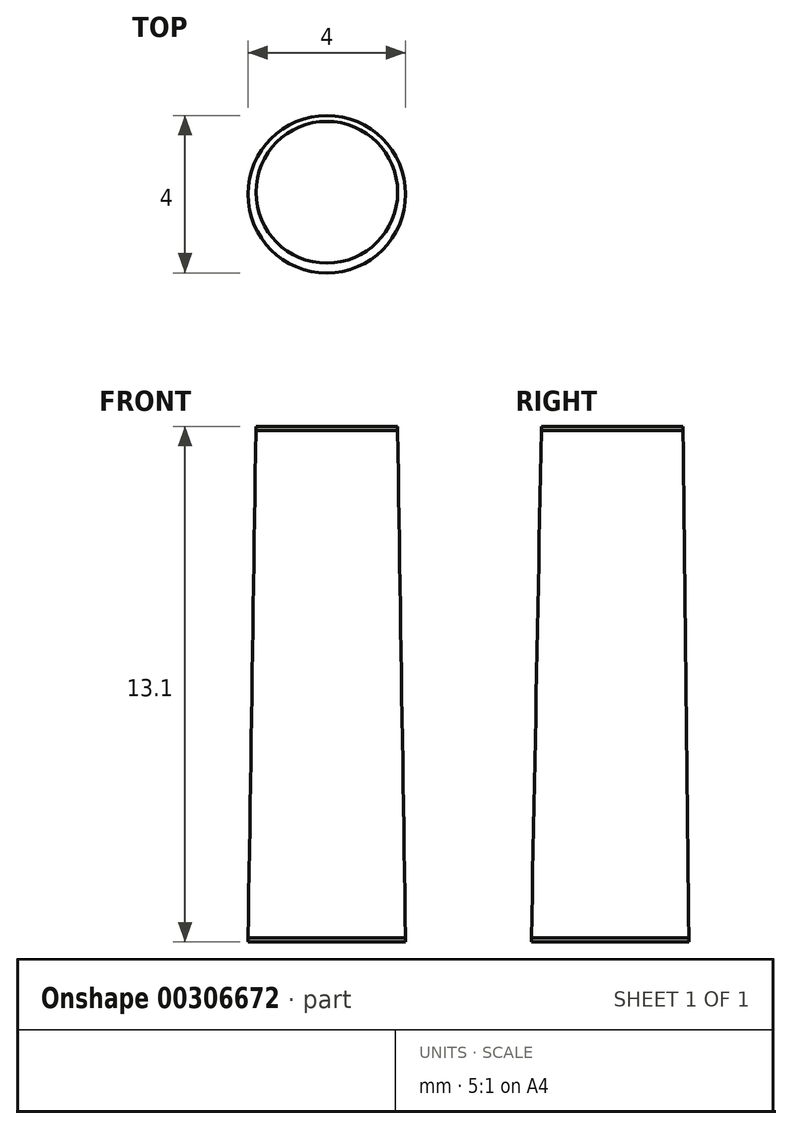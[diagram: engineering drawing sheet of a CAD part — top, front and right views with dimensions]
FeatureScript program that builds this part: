
annotation { "Feature Type Name" : "Feature", "Feature Type Description" : "" }
export const myFeature = defineFeature(function(context is Context, id is Id, definition is map)
    precondition{}
    {
        {
            var Q0;
            Q0=qCreatedBy(makeId("Top.planeOp"),FACE);
            var sketch = newSketch(context, id + "F0", { "sketchPlane" : qUnion([Q0])});
            skCircle(sketch, "E0", {"center": v(0, -0.05) * mm, "radius": 2 * mm});
            skSolve(sketch);
        }
        {
            var Q0;
            Q0=qCreatedBy(makeId("Top.planeOp"),FACE);
            var sketch = newSketch(context, id + "F1", { "sketchPlane" : qUnion([Q0])});
            skCircle(sketch, "E1", {"center": v(0, 0) * mm, "radius": 1.8 * mm});
            skSolve(sketch);
        }
        {
            var Q0;
            Q0=makeQuery(id+"F1.imprint","IMPRINT",FACE,{"disambiguationData":[TD([[makeQuery(id+"F1.imprint","IMPRINT",EDGE,{"derivedFrom":sQuery(id+"F1.wireOp",EDGE,"E1")}),1.0]])]});
            extrude(context, id + "F2", {"entities" : qUnion([Q0]), "depth" : 0.1 * mm});
        }
        {
            var Q0;
            Q0=makeQuery(id+"F2.opExtrude","SWEPT_BODY",BODY,{"disambiguationData":[OSD([sQuery(id+"F1.wireOp",EDGE,"E1")])]});
            transform(context, id + "F3", {"entities" : qUnion([Q0]), "transformType" : TransformType.TRANSLATION_3D, "dx" : 0 * mm, "dy" : 0 * mm, "dz" : 13 * mm, "makeCopy" : false});
        }
        {
            var Q0;
            Q0=makeQuery(id+"F0.imprint","IMPRINT",FACE,{"disambiguationData":[TD([[makeQuery(id+"F0.imprint","IMPRINT",EDGE,{"derivedFrom":sQuery(id+"F0.wireOp",EDGE,"E0")}),1.0]])]});
            var Q1;
            Q1 = qSketchRegion(id + "F0", true);
            extrude(context, id + "F4", {"entities" : qUnion([Q0, Q1]), "depth" : 0.1 * mm});
        }
        {
            var Q0;
            Q0=makeQuery(id+"F4.opExtrude","CAP_FACE",FACE,{"disambiguationData":[OSD([sQuery(id+"F0.wireOp",EDGE,"E0")])],"isStart":false});
            var Q1;
            Q1=makeQuery(id+"F2.opExtrude","CAP_FACE",FACE,{"disambiguationData":[OSD([sQuery(id+"F1.wireOp",EDGE,"E1")])],"isStart":true});
            loft(context, id + "F5", {"sheetProfilesArray" : [{ "sheetProfileEntities" : qUnion([Q0]) }, { "sheetProfileEntities" : qUnion([Q1]) }]});
        }
    });
